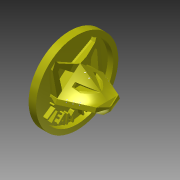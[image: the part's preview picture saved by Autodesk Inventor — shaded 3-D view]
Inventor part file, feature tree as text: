
AUTODESK INVENTOR PART (.ipt)
format: ipt  version: 2014 (Build 180170000, 170)  size: 1,200,128 bytes
history: native  units: in
note: dims shown in document units (in); Inventor stores cm internally (conversion verified against a paired STEP export)
features: sketch x23, extrude x16, plane x9, projected_geometry x6, loft x4, other x4, mirror x1, chamfer x1, fillet x1
ambient origin geometry x8: Origin, YZ Plane, XZ Plane, XY Plane, X Axis, Y Axis, Z Axis, Center Point
bodies: Solid1 (feature_tree)
feature tree (65):
  sketch  "Sketch1"  dims[d0=0.7559in d1=0.7559in]
  plane  "Work Plane1"
  loft  "Main Body"
  extrude  "Right Eye"  Depth=0.2in
  plane  "Work Plane4"
  loft  "Main Nose"
  plane  "Work Plane5"
  loft  "Back of Head"
  loft  "Main Ear - Right"
  extrude  "Inside of Ear - Right"  TaperAngle=0.0deg  [1 undecoded]
  plane  "Work Plane6"
  extrude  "Top and TopSide Rivets - Long"  Depth=1.0in
  extrude  "Top Most Rivet -  Cut Down"  Depth=1.0651in
  extrude  "Top Lower Rivet - Cut Down"  Depth=0.962in
  plane  "Work Plane7"
  extrude  "Side Rivets"  Depth=0.075in
  plane  "Work Plane8"
  other  "Work Axis1"
  plane  "Work Plane9"
  extrude  "Ear Shaping - Right"  Depth=0.06in
  mirror  "Eye, Ear and Rivet Mirro"
  extrude  "Fill Back (Make it a flat Print)"  Depth=0.05in
  plane  "Work Plane10"
  extrude  "Fill Back 2"  Depth=0.0625in
  plane  "Work Plane11"
  extrude  "Cut Back 1 (Adjust Angle)"  Depth=0.075in
  extrude  "Cut Back 2"  TaperAngle=0.0deg  [1 undecoded]
  extrude  "Round Back"  Depth=0.2in
  extrude  "Lip"  TaperAngle=0.0deg  [1 undecoded]
  other  "Team Text"
  extrude  "Remove Area for red backround"  Depth=0.01in
  extrude  "Remove Area for Ears"  Depth=0.0344in
  extrude  "Remove Area for Nose"  TaperAngle=60.0deg  [1 undecoded]
  chamfer  "Chamfer Eyes"  Distance=0.05in
  fillet  "Fill Bridge of Nose"  Radius=0.05in
  sketch  "Sketch2"  dims[d2=0.9963in d3=0.2in]
  sketch  "Sketch3"  dims[d4=0.5in d6=0.08in]
  sketch  "Sketch4"  dims[d7=0.55in d8=150.0deg]
  other  "Edges1"
  sketch  "Sketch5"  dims[d9=150.0deg d14=0.33in]
  projected_geometry  "Projected Loop1"
  other  "Edges2"
  sketch  "Sketch6"  dims[d15=0.66in d18=0.0in d19=90.0deg]
  sketch  "Sketch7"  dims[d20=0.0in d21=90.0deg d22=1.0in]
  sketch  "Sketch8"  dims[d26=1.0651in d28=1.0651in]
  sketch  "Sketch9"  dims[d29=0.0in d30=0.962in]
  sketch  "Sketch10"  dims[d31=0.962in d32=0.075in]
  sketch  "Sketch11"  dims[d33=0.15in d34=0.06in]
  sketch  "Sketch12"  dims[d35=0.1in d36=0.05in]
  sketch  "Sketch13"  dims[d37=0.45in d38=0.0in d39=0.0625in]
  projected_geometry  "Projected Loop2"
  projected_geometry  "Projected Loop3"
  sketch  "Sketch14"  dims[d40=0.01in d41=0.075in]
  projected_geometry  "Projected Loop4"
  sketch  "Sketch15"  dims[d42=0.01in d43=0.0in d44=90.0deg]
  sketch  "Sketch16"  dims[d45=0.0in d46=90.0deg d47=0.2in]
  sketch  "Sketch17"  dims[d48=0.07in d49=0.0in d50=90.0deg]
  sketch  "Sketch18"  dims[d51=0.0in d52=90.0deg d53=0.01in]
  sketch  "Sketch19"  dims[d54=0.01in d55=0.0344in]
  sketch  "Sketch20"  dims[d56=150.0deg d57=60.0deg]
  sketch  "Sketch22"  dims[d58=150.0deg]
  projected_geometry  "Projected Loop5"
  sketch  "Sketch23"  dims[d59=0.7in]
  projected_geometry  "Projected Loop6"
  sketch  "Sketch24"  dims[d60=0.05in d61=0.05in d62=0.05in d63=0.05in d64=0.05in d65=0.01in d66=0.0in d67=90.0deg d68=0.0in d69=90.0deg d70=0.1in d71=0.4in d72=0.15in d73=0.05in d74=0.0in d75=0.02in d77=0.15in d78=0.02in d79=0.1in d80=0.1in d81=0.1in d82=0.02in d83=0.15in d84=0.05in d85=0.0in d86=0.045in d87=0.0in d88=0.025in d89=0.0in d90=0.02in d91=0.02in d92=0.005in d93=0.0in d94=90.0deg d95=0.4466in d96=1.0in d97=0.0in d98=1.0in d99=0.0in d100=0.6528in d101=0.0in d102=0.0in d103=1.0in d104=0.0in d106=90.0deg d107=1.0in d108=0.0in d109=1.65in d110=0.1in d111=0.075in d112=0.0in d113=0.1in d114=0.075in d115=0.0in d116=0.05in d117=0.0in d121=0.0375in d122=0.0in d123=0.1in d124=0.0in d125=0.05in d126=0.0in d130=0.02in d131=0.125in d132=45.0deg d133=0.02in]
note: 4 required parameter values undecoded (feature->parameter linkage not recoverable at this tier; creation-order binding heuristic only, values carry confidence <= 0.55)
